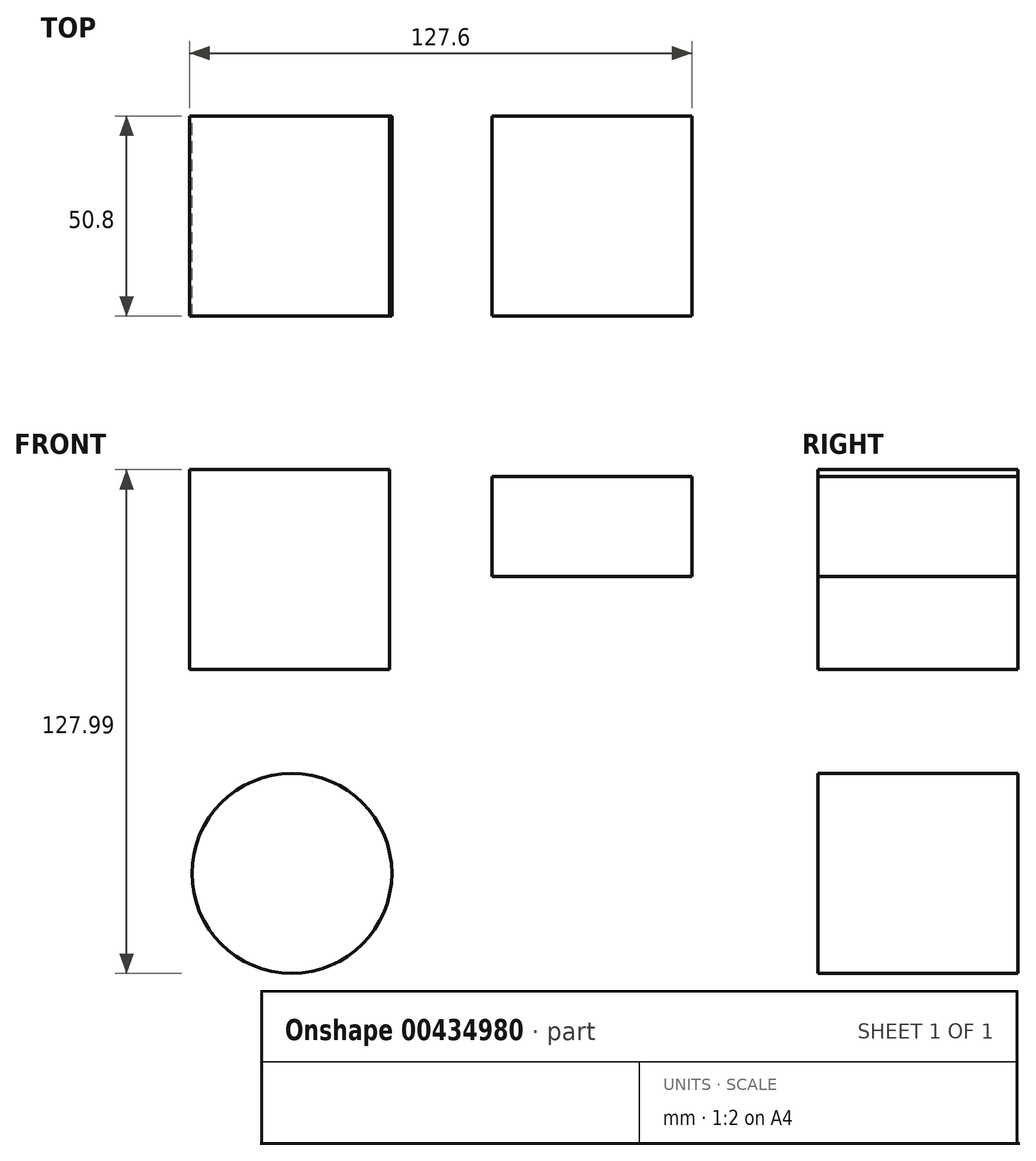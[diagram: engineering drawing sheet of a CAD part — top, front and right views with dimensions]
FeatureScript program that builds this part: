
annotation { "Feature Type Name" : "Feature", "Feature Type Description" : "" }
export const myFeature = defineFeature(function(context is Context, id is Id, definition is map)
    precondition{}
    {
        {
            var Q0;
            Q0=qCreatedBy(makeId("Front.planeOp"),FACE);
            var sketch = newSketch(context, id + "F0", { "sketchPlane" : qUnion([Q0])});
            skLineSegment(sketch, "E0.bottom", {"start": v(-12.98, 12.83) * mm, "end": v(-63.78, 12.83) * mm});
            skLineSegment(sketch, "E0.top", {"start": v(-12.98, 63.63) * mm, "end": v(-63.78, 63.63) * mm});
            skLineSegment(sketch, "E0.left", {"start": v(-12.98, 12.83) * mm, "end": v(-12.98, 63.63) * mm});
            skLineSegment(sketch, "E0.right", {"start": v(-63.78, 12.83) * mm, "end": v(-63.78, 63.63) * mm});
            skPoint(sketch, "E0.middle", {"position": v(-38.38, 38.23) * mm});
            skCircle(sketch, "E1", {"center": v(-37.81, -38.96) * mm, "radius": 25.4 * mm});
            skLineSegment(sketch, "E2.bottom", {"start": v(63.82, 36.47) * mm, "end": v(13.02, 36.47) * mm});
            skLineSegment(sketch, "E2.top", {"start": v(63.82, 61.87) * mm, "end": v(13.02, 61.87) * mm});
            skLineSegment(sketch, "E2.left", {"start": v(63.82, 36.47) * mm, "end": v(63.82, 61.87) * mm});
            skLineSegment(sketch, "E2.right", {"start": v(13.02, 36.47) * mm, "end": v(13.02, 61.87) * mm});
            skPoint(sketch, "E2.middle", {"position": v(38.42, 49.17) * mm});
            skSolve(sketch);
        }
        {
            var Q0;
            Q0 = qSketchRegion(id + "F0", true);
            extrude(context, id + "F1", {"entities" : qUnion([Q0]), "depth" : 50.8 * mm});
        }
    });
